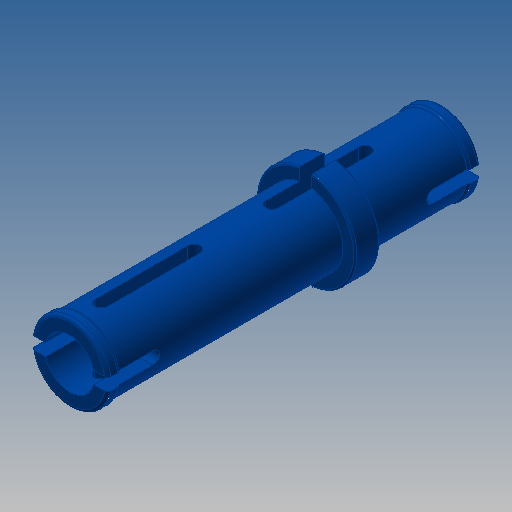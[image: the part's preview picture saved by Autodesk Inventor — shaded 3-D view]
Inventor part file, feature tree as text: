
AUTODESK INVENTOR PART (.ipt)
format: ipt  version: 2022.2 (Build 262287000, 287)  size: 303,104 bytes
history: native  units: mm (DEFAULTED — no unit token found)
features: sketch x2, extrude x2, revolve x1, fillet x1
ambient origin geometry x8: Origin, YZ Plane, XZ Plane, XY Plane, X Axis, Y Axis, Z Axis, Center Point
bodies: Solid2 (feature_tree)
feature tree (6):
  sketch  "Sketch1"  dims[d1=4.8mm d2=5.0mm d6=16.0mm]
  revolve  "Revolution1"  [1 undecoded]
  fillet  "Fillet1"  Radius=16.0mm
  extrude  "Extrusion1"  Depth=0.8mm
  extrude  "Extrusion2"  Depth=0.8mm
  sketch  "Sketch2"  dims[d7=0.8mm d8=6.4mm d9=0.8mm d10=0.8mm d14=0.8mm d16=6.8mm d17=0.8mm d18=2.0mm d19=8.0mm d20=90.0deg d21=10.0mm d22=0.0mm d25=10.0mm d26=0.0mm d27=0.2mm d28=0.1mm d29=0.0mm d30=0.0mm d31=3.2mm d32=3.4mm d33=0.8mm d34=3.4mm]
note: 1 required parameter value undecoded (feature->parameter linkage not recoverable at this tier; creation-order binding heuristic only, values carry confidence <= 0.55)
